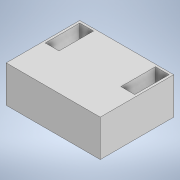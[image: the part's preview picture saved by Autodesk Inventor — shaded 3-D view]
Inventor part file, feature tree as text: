
AUTODESK INVENTOR PART (.ipt)
format: ipt  version: 2020 (Build 240168000, 168)  size: 108,032 bytes
history: native  units: mm
features: extrude x2, sketch x2
ambient origin geometry x8: Origin, YZ Plane, XZ Plane, XY Plane, X Axis, Y Axis, Z Axis, Center Point
bodies: Body1 (feature_tree)
feature tree (4):
  extrude  "Extrusão2"  Depth=80.0mm
  extrude  "Extrusão3"  TaperAngle=0.0deg  [1 undecoded]
  sketch  "Esboço3"  dims[d4=204.6mm d5=80.0mm]
  sketch  "Esboço7"  dims[d6=160.0mm d7=0.0mm d26=0.0mm d27=0.0mm]
note: 1 required parameter value undecoded (feature->parameter linkage not recoverable at this tier; creation-order binding heuristic only, values carry confidence <= 0.55)
